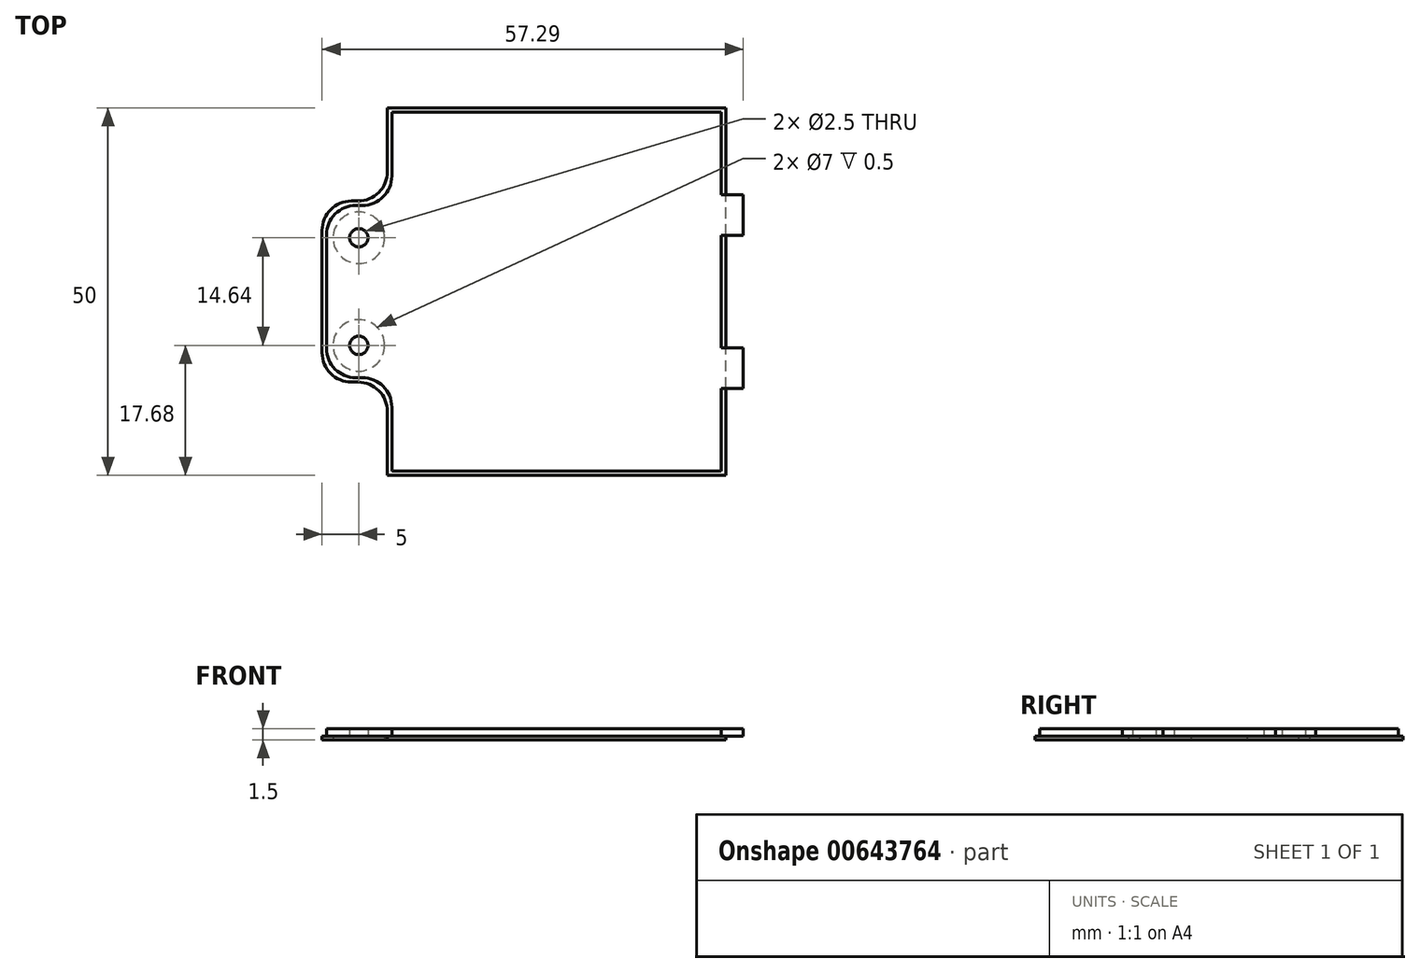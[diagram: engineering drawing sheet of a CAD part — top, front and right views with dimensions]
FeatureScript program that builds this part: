
annotation { "Feature Type Name" : "Feature", "Feature Type Description" : "" }
export const myFeature = defineFeature(function(context is Context, id is Id, definition is map)
    precondition{}
    {
        {
            var Q0;
            Q0=qCreatedBy(makeId("Top.planeOp"),FACE);
            var sketch = newSketch(context, id + "F0", { "sketchPlane" : qUnion([Q0])});
            skLineSegment(sketch, "E0.bottom", {"start": v(23, -25) * mm, "end": v(-23, -25) * mm});
            skLineSegment(sketch, "E0.top", {"start": v(23, 25) * mm, "end": v(-23, 25) * mm});
            skLineSegment(sketch, "E0.left", {"start": v(23, -25) * mm, "end": v(23, 25) * mm});
            skLineSegment(sketch, "E0.right", {"start": v(-23, -25) * mm, "end": v(-23, 25) * mm});
            skPoint(sketch, "E0.middle", {"position": v(0, 0) * mm});
            skLineSegment(sketch, "E1", {"start": v(0, 25) * mm, "end": v(0, -29.87) * mm, "construction": true});
            skPoint(sketch, "E1.endSnap0", {"position": v(0, 25) * mm});
            skLineSegment(sketch, "E2", {"start": v(-23, -25) * mm, "end": v(-23, -12.32) * mm, "construction": true});
            skLineSegment(sketch, "E3", {"start": v(-23, 25) * mm, "end": v(-23, 12.32) * mm, "construction": true});
            skLineSegment(sketch, "E4", {"start": v(-23, -12.32) * mm, "end": v(-31.9, -12.32) * mm});
            skLineSegment(sketch, "E5", {"start": v(-31.9, -12.32) * mm, "end": v(-31.9, 12.32) * mm});
            skLineSegment(sketch, "E6", {"start": v(-31.9, 12.32) * mm, "end": v(-23, 12.32) * mm});
            skSolve(sketch);
        }
        {
            var Q0;
            {var subQ1=sQuery(id+"F0.wireOp",EDGE,"E0.bottom");Q0=makeQuery(id+"F0.imprint","IMPRINT",FACE,{"disambiguationData":[TD([[makeQuery(id+"F0.imprint","IMPRINT",EDGE,{"derivedFrom":subQ1}),-1.0]])]});}
            var Q1;
            {var subQ0=sQuery(id+"F0.wireOp",EDGE,"E4");Q1=makeQuery(id+"F0.imprint","IMPRINT",FACE,{"disambiguationData":[TD([[makeQuery(id+"F0.imprint","IMPRINT",EDGE,{"derivedFrom":subQ0}),-1.0]])]});}
            extrude(context, id + "F1", {"entities" : qUnion([Q0, Q1]), "depth" : 0.5 * mm, "offsetDistance" : 25 * mm});
        }
        {
            var Q0;
            Q0=makeQuery(id+"F1.opExtrude","CAP_FACE",FACE,{"disambiguationData":[OSD([sQuery(id+"F0.wireOp",EDGE,"E0.bottom"),sQuery(id+"F0.wireOp",EDGE,"E0.top"),sQuery(id+"F0.wireOp",EDGE,"E0.left"),sQuery(id+"F0.wireOp",EDGE,"E0.right"),sQuery(id+"F0.wireOp",EDGE,"E4"),sQuery(id+"F0.wireOp",EDGE,"E5"),sQuery(id+"F0.wireOp",EDGE,"E6")])],"isStart":false});
            var sketch = newSketch(context, id + "F2", { "sketchPlane" : qUnion([Q0])});
            skLineSegment(sketch, "E7.0", {"start": v(22.4, -24.4) * mm, "end": v(22.4, 24.4) * mm});
            skLineSegment(sketch, "E7.1", {"start": v(22.4, -24.4) * mm, "end": v(-22.4, -24.4) * mm});
            skLineSegment(sketch, "E7.2", {"start": v(22.4, 24.4) * mm, "end": v(-22.4, 24.4) * mm});
            skLineSegment(sketch, "E7.3", {"start": v(-22.4, -24.4) * mm, "end": v(-22.4, -11.72) * mm});
            skLineSegment(sketch, "E7.4", {"start": v(-22.4, 11.72) * mm, "end": v(-22.4, 24.4) * mm});
            skLineSegment(sketch, "E7.5", {"start": v(-31.3, 11.72) * mm, "end": v(-22.4, 11.72) * mm});
            skLineSegment(sketch, "E7.6", {"start": v(-31.3, -11.72) * mm, "end": v(-31.3, 11.72) * mm});
            skLineSegment(sketch, "E7.7", {"start": v(-22.4, -11.72) * mm, "end": v(-31.3, -11.72) * mm});
            skSolve(sketch);
        }
        {
            var Q0;
            Q0=makeQuery(id+"F2.imprint","IMPRINT",FACE,{"disambiguationData":[TD([[makeQuery(id+"F2.imprint","IMPRINT",EDGE,{"derivedFrom":sQuery(id+"F2.wireOp",EDGE,"E7.0")}),1.0]])]});
            extrude(context, id + "F3", {"entities" : qUnion([Q0]), "operationType" : NewBodyOperationType.ADD, "depth" : 1 * mm, "offsetDistance" : 25 * mm});
        }
        {
            var Q0;
            Q0=makeQuery(id+"F1.opExtrude","SWEPT_EDGE",EDGE,{"disambiguationData":[OSD([sQuery(id+"F0.wireOp",EDGE,"E5"),sQuery(id+"F0.wireOp",EDGE,"E6")])]});
            var Q1;
            Q1=makeQuery(id+"F3.opExtrude","SWEPT_EDGE",EDGE,{"disambiguationData":[OSD([sQuery(id+"F2.wireOp",EDGE,"E7.5"),sQuery(id+"F2.wireOp",EDGE,"E7.6")])]});
            var Q2;
            Q2=makeQuery(id+"F1.opExtrude","SWEPT_EDGE",EDGE,{"disambiguationData":[OSD([sQuery(id+"F0.wireOp",EDGE,"E0.right"),sQuery(id+"F0.wireOp",EDGE,"E6")])]});
            var Q3;
            Q3=makeQuery(id+"F3.opExtrude","SWEPT_EDGE",EDGE,{"disambiguationData":[OSD([sQuery(id+"F2.wireOp",EDGE,"E7.4"),sQuery(id+"F2.wireOp",EDGE,"E7.5")])]});
            var Q4;
            Q4=makeQuery(id+"F3.opExtrude","SWEPT_EDGE",EDGE,{"disambiguationData":[OSD([sQuery(id+"F2.wireOp",EDGE,"E7.6"),sQuery(id+"F2.wireOp",EDGE,"E7.7")])]});
            var Q5;
            Q5=makeQuery(id+"F1.opExtrude","SWEPT_EDGE",EDGE,{"disambiguationData":[OSD([sQuery(id+"F0.wireOp",EDGE,"E4"),sQuery(id+"F0.wireOp",EDGE,"E5")])]});
            var Q6;
            Q6=makeQuery(id+"F1.opExtrude","SWEPT_EDGE",EDGE,{"disambiguationData":[OSD([sQuery(id+"F0.wireOp",EDGE,"E0.right"),sQuery(id+"F0.wireOp",EDGE,"E4")])]});
            var Q7;
            Q7=makeQuery(id+"F3.opExtrude","SWEPT_EDGE",EDGE,{"disambiguationData":[OSD([sQuery(id+"F2.wireOp",EDGE,"E7.3"),sQuery(id+"F2.wireOp",EDGE,"E7.7")])]});
            fillet(context, id + "F4", {"entities" : qUnion([Q0, Q1, Q2, Q3, Q4, Q5, Q6, Q7]), "radius" : 4 * mm, "tangentPropagation" : true, "allowEdgeOverflow" : false});
        }
        {
            var Q0;
            Q0=makeQuery(id+"F1.opExtrude","CAP_FACE",FACE,{"disambiguationData":[OSD([sQuery(id+"F0.wireOp",EDGE,"E0.bottom"),sQuery(id+"F0.wireOp",EDGE,"E0.top"),sQuery(id+"F0.wireOp",EDGE,"E0.left"),sQuery(id+"F0.wireOp",EDGE,"E0.right"),sQuery(id+"F0.wireOp",EDGE,"E4"),sQuery(id+"F0.wireOp",EDGE,"E5"),sQuery(id+"F0.wireOp",EDGE,"E6")])],"isStart":true});
            var sketch = newSketch(context, id + "F5", { "sketchPlane" : qUnion([Q0])});
            skPoint(sketch, "E8.endSnap0", {"position": v(-26.9, 12.32) * mm});
            skPoint(sketch, "E9", {"position": v(-26.9, -7.32) * mm});
            skPoint(sketch, "E10", {"position": v(-26.9, 7.32) * mm});
            skSolve(sketch);
        }
        {
            var Q0;
            Q0=sQuery(id+"F5.wireOp",VERTEX,"E9");
            var Q1;
            Q1=sQuery(id+"F5.wireOp",VERTEX,"E10");
            var Q2;
            Q2=makeQuery(id+"F1.opExtrude","SWEPT_BODY",BODY,{"disambiguationData":[OSD([sQuery(id+"F0.wireOp",EDGE,"E0.bottom"),sQuery(id+"F0.wireOp",EDGE,"E0.top"),sQuery(id+"F0.wireOp",EDGE,"E0.left"),sQuery(id+"F0.wireOp",EDGE,"E0.right"),sQuery(id+"F0.wireOp",EDGE,"E4"),sQuery(id+"F0.wireOp",EDGE,"E5"),sQuery(id+"F0.wireOp",EDGE,"E6")])]});
            hole(context, id + "F6", {"style" : HoleStyle.C_BORE, "endStyle" : HoleEndStyle.THROUGH, "holeDiameter" : 2.5 * mm, "cBoreDiameter" : 7 * mm, "cBoreDepth" : 0.5 * mm, "majorDiameter" : 5 * mm, "isTappedThrough" : true, "tappedDepth" : 12 * mm, "tapClearance" : 3, "locations" : qUnion([Q0, Q1]), "scope" : qUnion([Q2])});
        }
        {
            var Q0;
            Q0=makeQuery(id+"F3.opExtrude","SWEPT_FACE",FACE,{"disambiguationData":[OSD([sQuery(id+"F2.wireOp",EDGE,"E7.0")])]});
            var sketch = newSketch(context, id + "F7", { "sketchPlane" : qUnion([Q0])});
            skLineSegment(sketch, "E11", {"start": v(-13.15, 0.5) * mm, "end": v(-13.15, 1.5) * mm});
            skLineSegment(sketch, "E12", {"start": v(13.15, 0.5) * mm, "end": v(13.15, 1.5) * mm});
            skLineSegment(sketch, "E13", {"start": v(-7.65, 0.5) * mm, "end": v(-7.65, 1.5) * mm});
            skLineSegment(sketch, "E14", {"start": v(7.65, 0.5) * mm, "end": v(7.65, 1.5) * mm});
            skSolve(sketch);
        }
        {
            var Q0;
            {var subQ0=sQuery(id+"F7.wireOp",EDGE,"E11");Q0=makeQuery(id+"F7.imprint","IMPRINT",FACE,{"disambiguationData":[TD([[makeQuery(id+"F7.imprint","IMPRINT",EDGE,{"derivedFrom":subQ0}),-1.0]])]});}
            var Q1;
            {var subQ0=sQuery(id+"F7.wireOp",EDGE,"E12");Q1=makeQuery(id+"F7.imprint","IMPRINT",FACE,{"disambiguationData":[TD([[makeQuery(id+"F7.imprint","IMPRINT",EDGE,{"derivedFrom":subQ0}),1.0]])]});}
            extrude(context, id + "F8", {"entities" : qUnion([Q0, Q1]), "operationType" : NewBodyOperationType.ADD, "depth" : 3 * mm, "offsetDistance" : 25 * mm});
        }
    });
